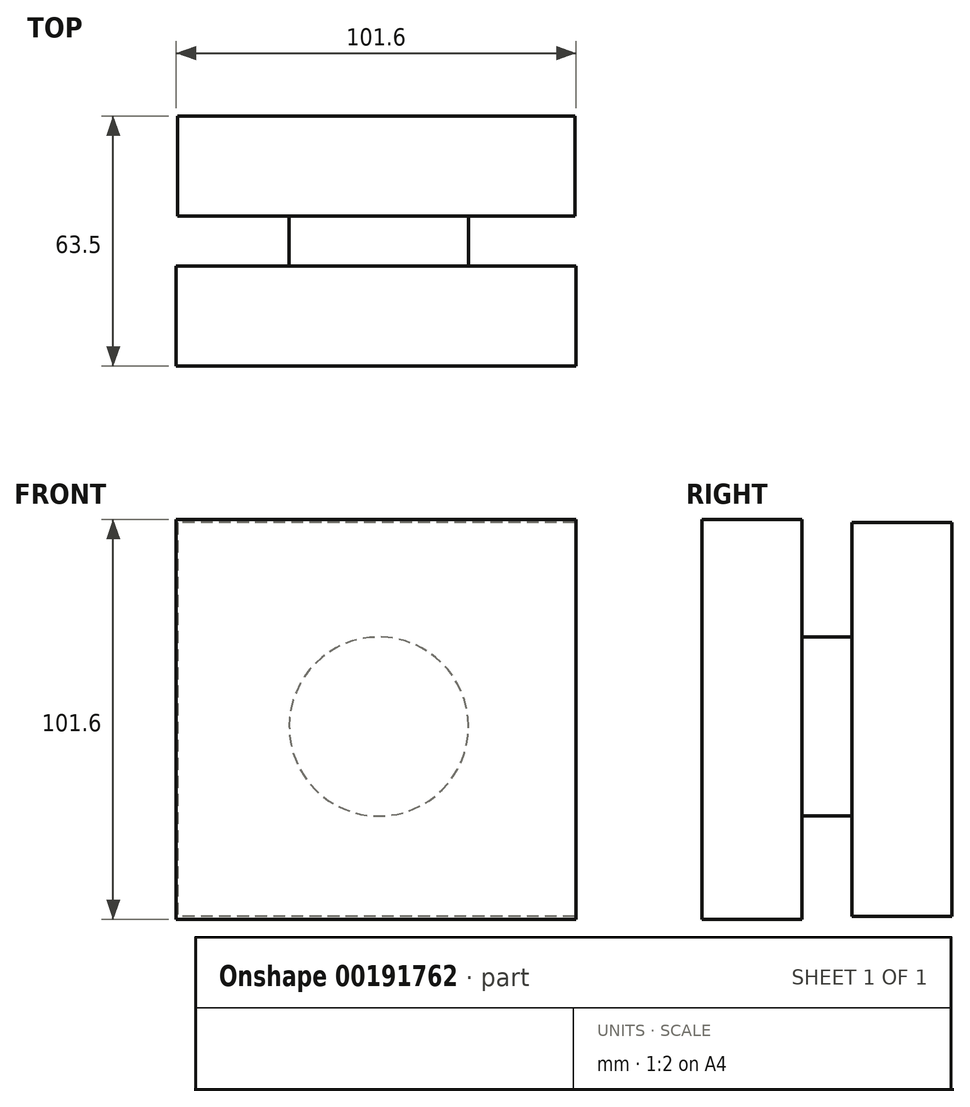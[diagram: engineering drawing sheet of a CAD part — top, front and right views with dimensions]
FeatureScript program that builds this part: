
annotation { "Feature Type Name" : "Feature", "Feature Type Description" : "" }
export const myFeature = defineFeature(function(context is Context, id is Id, definition is map)
    precondition{}
    {
        {
            var Q0;
            Q0=qCreatedBy(makeId("Front.planeOp"),FACE);
            var sketch = newSketch(context, id + "F0", { "sketchPlane" : qUnion([Q0])});
            skLineSegment(sketch, "E0.bottom", {"start": v(-57.56, 57.56) * mm, "end": v(44.04, 57.56) * mm});
            skLineSegment(sketch, "E0.top", {"start": v(-57.56, -44.04) * mm, "end": v(44.04, -44.04) * mm});
            skLineSegment(sketch, "E0.left", {"start": v(-57.56, 57.56) * mm, "end": v(-57.56, -44.04) * mm});
            skLineSegment(sketch, "E0.right", {"start": v(44.04, 57.56) * mm, "end": v(44.04, -44.04) * mm});
            skSolve(sketch);
        }
        {
            var Q0;
            Q0=makeQuery(id+"F0.imprint","IMPRINT",FACE,{"disambiguationData":[TD([[makeQuery(id+"F0.imprint","IMPRINT",EDGE,{"derivedFrom":sQuery(id+"F0.wireOp",EDGE,"E0.bottom")}),-1.0]])]});
            extrude(context, id + "F1", {"entities" : qUnion([Q0]), "depth" : 25.4 * mm});
        }
        {
            var Q0;
            Q0=makeQuery(id+"F1.opExtrude","CAP_FACE",FACE,{"disambiguationData":[OSD([sQuery(id+"F0.wireOp",EDGE,"E0.bottom"),sQuery(id+"F0.wireOp",EDGE,"E0.top"),sQuery(id+"F0.wireOp",EDGE,"E0.left"),sQuery(id+"F0.wireOp",EDGE,"E0.right")])],"isStart":true});
            var sketch = newSketch(context, id + "F2", { "sketchPlane" : qUnion([Q0])});
            skCircle(sketch, "E1", {"center": v(6.09, 4.96) * mm, "radius": 22.75 * mm});
            skSolve(sketch);
        }
        {
            var Q0;
            Q0 = qSketchRegion(id + "F2", true);
            extrude(context, id + "F3", {"entities" : qUnion([Q0]), "operationType" : NewBodyOperationType.ADD, "depth" : 12.7 * mm});
        }
        {
            var Q0;
            Q0=makeQuery(id+"F3.opExtrude","CAP_FACE",FACE,{"disambiguationData":[OSD([sQuery(id+"F2.wireOp",EDGE,"E1")])],"isStart":false});
            var sketch = newSketch(context, id + "F4", { "sketchPlane" : qUnion([Q0])});
            skLineSegment(sketch, "E2.bottom", {"start": v(-43.71, 56.79) * mm, "end": v(57.24, 56.79) * mm});
            skLineSegment(sketch, "E2.top", {"start": v(-43.71, -43.27) * mm, "end": v(57.24, -43.27) * mm});
            skLineSegment(sketch, "E2.left", {"start": v(-43.71, 56.79) * mm, "end": v(-43.71, -43.27) * mm});
            skLineSegment(sketch, "E2.right", {"start": v(57.24, 56.79) * mm, "end": v(57.24, -43.27) * mm});
            skSolve(sketch);
        }
        {
            var Q0;
            Q0 = qSketchRegion(id + "F4", true);
            extrude(context, id + "F5", {"entities" : qUnion([Q0]), "depth" : 25.4 * mm});
        }
    });
